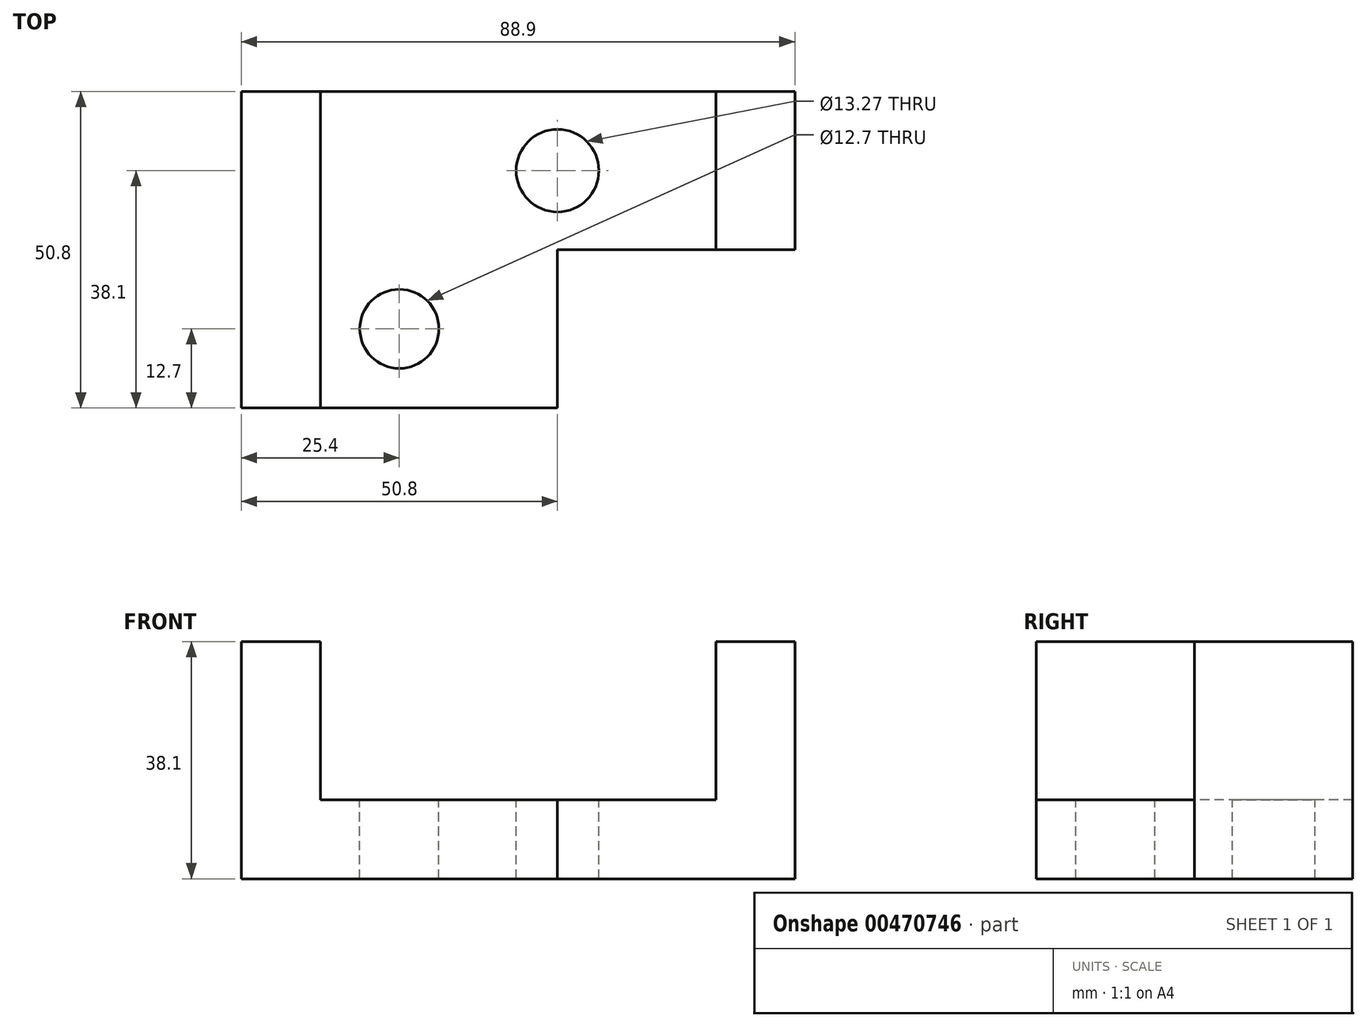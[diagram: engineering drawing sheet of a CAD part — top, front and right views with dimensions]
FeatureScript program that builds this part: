
annotation { "Feature Type Name" : "Feature", "Feature Type Description" : "" }
export const myFeature = defineFeature(function(context is Context, id is Id, definition is map)
    precondition{}
    {
        {
            var Q0;
            Q0=qCreatedBy(makeId("Front.planeOp"),FACE);
            var sketch = newSketch(context, id + "F0", { "sketchPlane" : qUnion([Q0])});
            skLineSegment(sketch, "E0.bottom", {"start": v(44.45, -19.05) * mm, "end": v(-44.45, -19.05) * mm});
            skLineSegment(sketch, "E0.top", {"start": v(44.45, 19.05) * mm, "end": v(-44.45, 19.05) * mm});
            skLineSegment(sketch, "E0.left", {"start": v(44.45, -19.05) * mm, "end": v(44.45, 19.05) * mm});
            skLineSegment(sketch, "E0.right", {"start": v(-44.45, -19.05) * mm, "end": v(-44.45, 19.05) * mm});
            skPoint(sketch, "E0.middle", {"position": v(0, 0) * mm});
            skSolve(sketch);
        }
        {
            var Q0;
            Q0 = qSketchRegion(id + "F0", true);
            extrude(context, id + "F1", {"entities" : qUnion([Q0]), "depth" : 50.8 * mm});
        }
        {
            var Q0;
            Q0=makeQuery(id+"F1.opExtrude","SWEPT_FACE",FACE,{"disambiguationData":[OSD([sQuery(id+"F0.wireOp",EDGE,"E0.top")])]});
            var sketch = newSketch(context, id + "F2", { "sketchPlane" : qUnion([Q0])});
            skLineSegment(sketch, "E1.bottom", {"start": v(44.45, -50.8) * mm, "end": v(6.35, -50.8) * mm});
            skLineSegment(sketch, "E1.top", {"start": v(44.45, -25.4) * mm, "end": v(6.35, -25.4) * mm});
            skLineSegment(sketch, "E1.left", {"start": v(44.45, -50.8) * mm, "end": v(44.45, -25.4) * mm});
            skLineSegment(sketch, "E1.right", {"start": v(6.35, -50.8) * mm, "end": v(6.35, -25.4) * mm});
            skSolve(sketch);
        }
        {
            var Q0;
            Q0 = qSketchRegion(id + "F2", true);
            extrude(context, id + "F3", {"entities" : qUnion([Q0]), "operationType" : NewBodyOperationType.REMOVE, "endBound" : BoundingType.THROUGH_ALL, "oppositeDirection" : true, "depth" : 25.4 * mm});
        }
        {
            var Q0;
            Q0=makeQuery(id+"F1.opExtrude","CAP_FACE",FACE,{"disambiguationData":[OSD([sQuery(id+"F0.wireOp",EDGE,"E0.bottom"),sQuery(id+"F0.wireOp",EDGE,"E0.top"),sQuery(id+"F0.wireOp",EDGE,"E0.left"),sQuery(id+"F0.wireOp",EDGE,"E0.right")])],"isStart":false});
            var sketch = newSketch(context, id + "F4", { "sketchPlane" : qUnion([Q0])});
            skLineSegment(sketch, "E2.bottom", {"start": v(-31.75, 19.05) * mm, "end": v(31.75, 19.05) * mm});
            skLineSegment(sketch, "E2.top", {"start": v(-31.75, -6.35) * mm, "end": v(31.75, -6.35) * mm});
            skLineSegment(sketch, "E2.left", {"start": v(-31.75, 19.05) * mm, "end": v(-31.75, -6.35) * mm});
            skLineSegment(sketch, "E2.right", {"start": v(31.75, 19.05) * mm, "end": v(31.75, -6.35) * mm});
            skSolve(sketch);
        }
        {
            var Q0;
            Q0 = qSketchRegion(id + "F4", true);
            extrude(context, id + "F5", {"entities" : qUnion([Q0]), "operationType" : NewBodyOperationType.REMOVE, "endBound" : BoundingType.THROUGH_ALL, "oppositeDirection" : true, "depth" : 25.4 * mm});
        }
        {
            var Q0;
            Q0=makeQuery(id+"F5.boolean.opBoolean","COPY",FACE,{"derivedFrom":makeQuery(id+"F5.opExtrude","SWEPT_FACE",FACE,{"disambiguationData":[OSD([sQuery(id+"F4.wireOp",EDGE,"E2.top")])]})});
            var sketch = newSketch(context, id + "F6", { "sketchPlane" : qUnion([Q0])});
            skCircle(sketch, "E3", {"center": v(-19.05, -38.1) * mm, "radius": 6.35 * mm});
            skCircle(sketch, "E4", {"center": v(6.35, -12.7) * mm, "radius": 6.64 * mm});
            skSolve(sketch);
        }
        {
            var Q0;
            Q0 = qSketchRegion(id + "F6", true);
            extrude(context, id + "F7", {"entities" : qUnion([Q0]), "operationType" : NewBodyOperationType.REMOVE, "endBound" : BoundingType.THROUGH_ALL, "oppositeDirection" : true, "depth" : 25.4 * mm});
        }
    });
